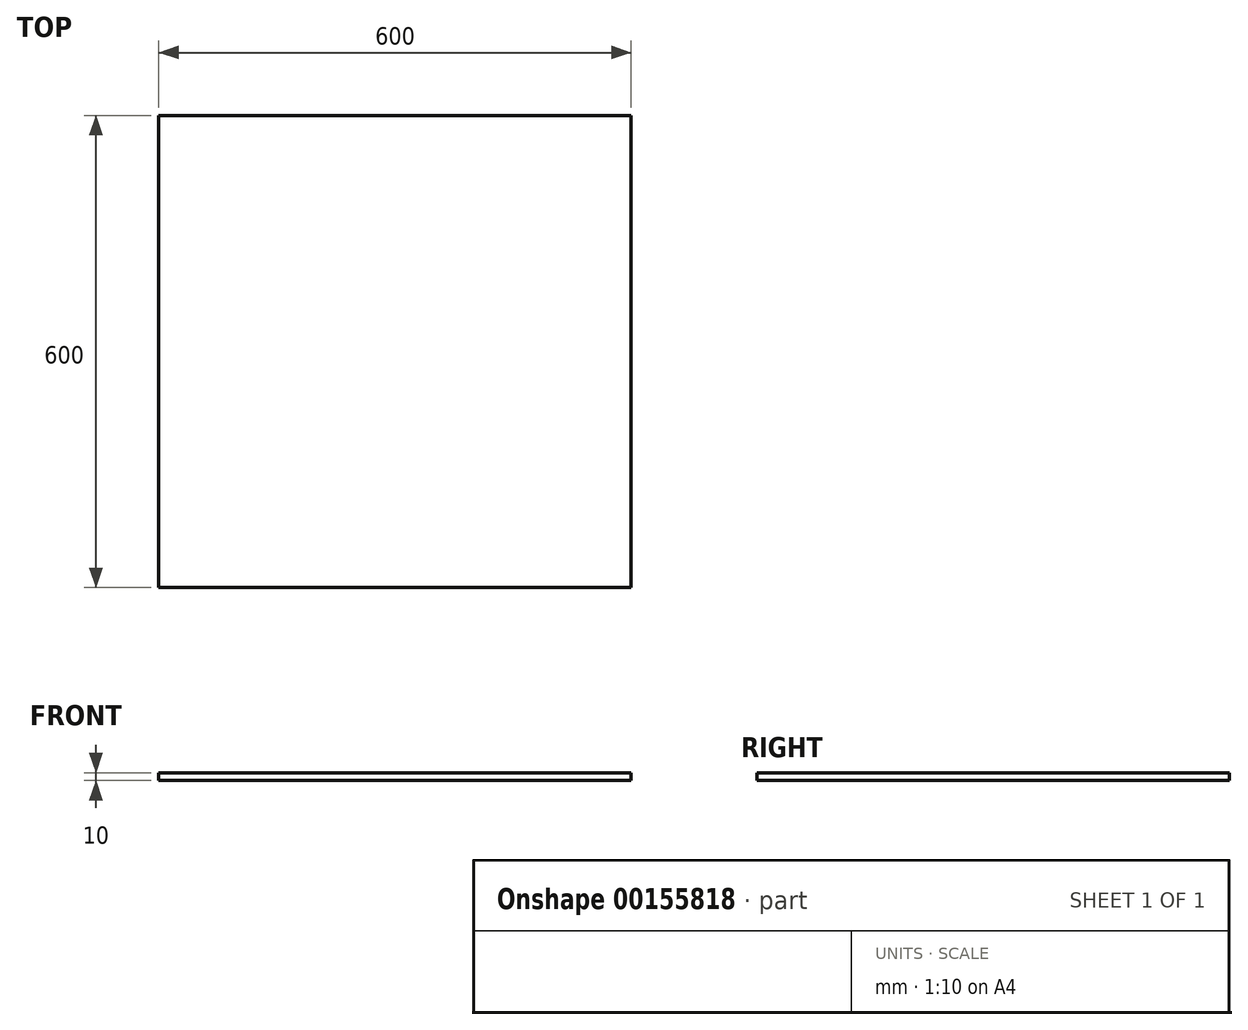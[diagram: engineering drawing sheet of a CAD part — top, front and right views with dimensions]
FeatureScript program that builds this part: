
annotation { "Feature Type Name" : "Feature", "Feature Type Description" : "" }
export const myFeature = defineFeature(function(context is Context, id is Id, definition is map)
    precondition{}
    {
        {
            var Q0;
            Q0=qCreatedBy(makeId("Top.planeOp"),FACE);
            var sketch = newSketch(context, id + "F0", { "sketchPlane" : qUnion([Q0])});
            skLineSegment(sketch, "E0.bottom", {"start": v(-300, 300) * mm, "end": v(300, 300) * mm});
            skLineSegment(sketch, "E0.top", {"start": v(-300, -300) * mm, "end": v(300, -300) * mm});
            skLineSegment(sketch, "E0.left", {"start": v(-300, 300) * mm, "end": v(-300, -300) * mm});
            skLineSegment(sketch, "E0.right", {"start": v(300, 300) * mm, "end": v(300, -300) * mm});
            skPoint(sketch, "E0.middle", {"position": v(0, 0) * mm});
            skSolve(sketch);
        }
        {
            var Q0;
            Q0=makeQuery(id+"F0.imprint","IMPRINT",FACE,{"disambiguationData":[TD([[makeQuery(id+"F0.imprint","IMPRINT",EDGE,{"derivedFrom":sQuery(id+"F0.wireOp",EDGE,"E0.bottom")}),-1.0]])]});
            extrude(context, id + "F1", {"entities" : qUnion([Q0]), "depth" : 10 * mm});
        }
    });
